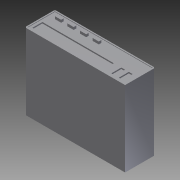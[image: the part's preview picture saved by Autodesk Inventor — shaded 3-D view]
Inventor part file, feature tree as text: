
AUTODESK INVENTOR PART (.ipt)
format: ipt  version: 2012 (Build 160160000, 160)  size: 158,720 bytes
history: native  units: in
note: dims shown in document units (in); Inventor stores cm internally (conversion verified against a paired STEP export)
features: extrude x4, sketch x4, pattern_linear x1, chamfer x1
ambient origin geometry x8: Origin, YZ Plane, XZ Plane, XY Plane, X Axis, Y Axis, Z Axis, Center Point
bodies: Solid1 (feature_tree)
feature tree (10):
  extrude  "Extrusion1"  Depth=11.811in
  extrude  "Extrusion2"  Depth=4.7244in
  pattern_linear  "Rectangular Pattern1"  Count1=12 Spacing1=0.0in
  extrude  "Extrusion3"  Depth=0.3937in
  chamfer  "Chamfer1"  Distance=8.6614in
  extrude  "Extrusion4"  Depth=0.3937in TaperAngle=0.0deg
  sketch  "Sketch1"  dims[d0=1.9685in d1=11.811in]
  sketch  "Sketch2"  dims[d2=15.748in d3=4.7244in d4=4.7244in d5=0.0in]
  sketch  "Sketch3"  dims[d6=0.9843in d7=0.3937in]
  sketch  "Sketch4"  dims[d8=0.7874in d9=8.6614in d10=0.3937in d11=0.0in d12=1.5748in d14=1.9685in d15=2.5591in d16=0.5906in d17=0.5906in d18=3.937in d19=0.1969in d20=0.0in d21=1.1811in d22=0.5906in d23=0.5906in d24=0.1575in d25=0.0787in d26=45.0deg d27=0.0787in d28=0.0in]
